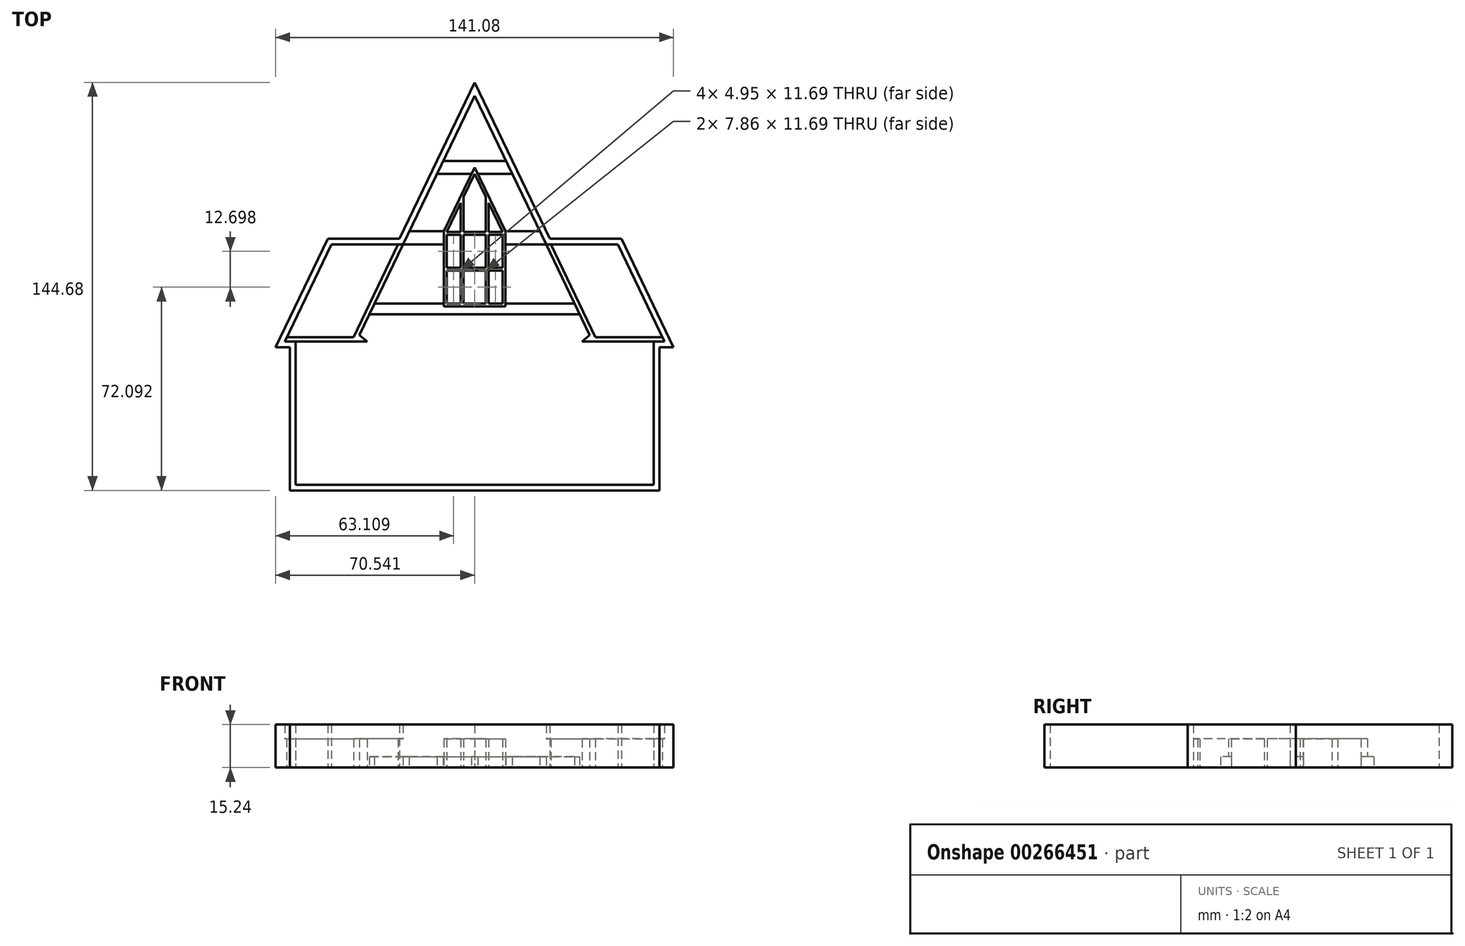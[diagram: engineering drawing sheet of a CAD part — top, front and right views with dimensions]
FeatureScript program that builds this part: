
annotation { "Feature Type Name" : "Feature", "Feature Type Description" : "" }
export const myFeature = defineFeature(function(context is Context, id is Id, definition is map)
    precondition{}
    {
        {
            var Q0;
            Q0=qCreatedBy(makeId("Top.planeOp"),FACE);
            var sketch = newSketch(context, id + "F0", { "sketchPlane" : qUnion([Q0])});
            skLineSegment(sketch, "E0", {"start": v(-58.74, -50.8) * mm, "end": v(68.26, -50.8) * mm});
            skLineSegment(sketch, "E1", {"start": v(-58.74, -50.8) * mm, "end": v(-58.74, 0) * mm});
            skLineSegment(sketch, "E2", {"start": v(68.26, -50.8) * mm, "end": v(68.26, 0) * mm});
            skLineSegment(sketch, "E3", {"start": v(-61.82, 1.52) * mm, "end": v(-46.04, 34.34) * mm});
            skLineSegment(sketch, "E4", {"start": v(-46.04, 34.34) * mm, "end": v(-22.33, 34.34) * mm});
            skLineSegment(sketch, "E5", {"start": v(71.34, 1.52) * mm, "end": v(55.56, 34.34) * mm});
            skLineSegment(sketch, "E6", {"start": v(55.56, 34.34) * mm, "end": v(30.16, 34.34) * mm});
            skLineSegment(sketch, "E7", {"start": v(-20.64, 34.34) * mm, "end": v(-36.05, 2.29) * mm});
            skLineSegment(sketch, "E8", {"start": v(30.16, 34.34) * mm, "end": v(45.57, 2.29) * mm});
            skLineSegment(sketch, "E9", {"start": v(68.26, 0) * mm, "end": v(42.86, 0) * mm});
            skLineSegment(sketch, "E10", {"start": v(42.86, 0) * mm, "end": v(45.57, 2.29) * mm});
            skLineSegment(sketch, "E11", {"start": v(-58.74, 0) * mm, "end": v(-33.34, 0) * mm});
            skLineSegment(sketch, "E12", {"start": v(-33.34, 0) * mm, "end": v(-36.05, 2.29) * mm});
            skLineSegment(sketch, "E13", {"start": v(30.16, 34.34) * mm, "end": v(4.76, 87.16) * mm});
            skLineSegment(sketch, "E14", {"start": v(4.76, 87.16) * mm, "end": v(-20.64, 34.34) * mm});
            skLineSegment(sketch, "E15", {"start": v(4.76, 59.42) * mm, "end": v(0.83, 51.25) * mm});
            skLineSegment(sketch, "E16", {"start": v(4.76, 59.42) * mm, "end": v(8.7, 51.24) * mm});
            skLineSegment(sketch, "E17", {"start": v(14.66, 37.8) * mm, "end": v(14.66, 26.12) * mm});
            skLineSegment(sketch, "E18", {"start": v(-5.15, 37.8) * mm, "end": v(-5.15, 26.12) * mm});
            skLineSegment(sketch, "E19", {"start": v(-5.15, 13.42) * mm, "end": v(-0.2, 13.42) * mm});
            skLineSegment(sketch, "E20", {"start": v(9.71, 13.42) * mm, "end": v(9.71, 25.1) * mm});
            skLineSegment(sketch, "E21", {"start": v(-0.2, 49.12) * mm, "end": v(-0.2, 38.82) * mm});
            skLineSegment(sketch, "E22", {"start": v(14.66, 26.12) * mm, "end": v(9.71, 26.12) * mm});
            skLineSegment(sketch, "E23", {"start": v(14.66, 38.82) * mm, "end": v(9.71, 38.82) * mm});
            skLineSegment(sketch, "E24.0", {"start": v(-58.74, 1.52) * mm, "end": v(-38.11, 1.52) * mm});
            skLineSegment(sketch, "E24.1", {"start": v(-22.33, 34.34) * mm, "end": v(-38.11, 1.52) * mm});
            skLineSegment(sketch, "E25", {"start": v(-58.74, 1.52) * mm, "end": v(-61.82, 1.52) * mm});
            skLineSegment(sketch, "E26.0", {"start": v(68.26, 1.52) * mm, "end": v(47.63, 1.52) * mm});
            skLineSegment(sketch, "E26.1", {"start": v(31.85, 34.34) * mm, "end": v(47.63, 1.52) * mm});
            skLineSegment(sketch, "E27", {"start": v(68.26, 1.52) * mm, "end": v(71.34, 1.52) * mm});
            skLineSegment(sketch, "E28", {"start": v(-22.33, 34.34) * mm, "end": v(-20.64, 34.34) * mm});
            skLineSegment(sketch, "E29", {"start": v(-61.82, 1.52) * mm, "end": v(-62.55, 0) * mm});
            skLineSegment(sketch, "E30", {"start": v(-62.55, 0) * mm, "end": v(-58.74, 0) * mm});
            skLineSegment(sketch, "E31", {"start": v(71.34, 1.52) * mm, "end": v(72.07, 0) * mm});
            skLineSegment(sketch, "E32", {"start": v(68.26, 0) * mm, "end": v(72.07, 0) * mm});
            skLineSegment(sketch, "E33.0", {"start": v(31.44, 36.37) * mm, "end": v(4.76, 91.85) * mm});
            skLineSegment(sketch, "E33.1", {"start": v(56.84, 36.37) * mm, "end": v(31.44, 36.37) * mm});
            skLineSegment(sketch, "E33.2", {"start": v(72.68, 3.42) * mm, "end": v(56.84, 36.37) * mm});
            skLineSegment(sketch, "E33.3", {"start": v(-63.16, 3.42) * mm, "end": v(-65.78, -2.03) * mm});
            skLineSegment(sketch, "E33.4", {"start": v(-63.16, 3.42) * mm, "end": v(-47.32, 36.37) * mm});
            skLineSegment(sketch, "E33.5", {"start": v(-47.32, 36.37) * mm, "end": v(-23.46, 36.37) * mm});
            skLineSegment(sketch, "E33.6", {"start": v(-23.46, 36.37) * mm, "end": v(-21.92, 36.37) * mm});
            skLineSegment(sketch, "E33.7", {"start": v(-65.78, -2.03) * mm, "end": v(-60.77, -2.03) * mm});
            skLineSegment(sketch, "E33.8", {"start": v(-60.77, -52.83) * mm, "end": v(-60.77, -2.03) * mm});
            skLineSegment(sketch, "E33.9", {"start": v(-60.77, -52.83) * mm, "end": v(70.3, -52.83) * mm});
            skLineSegment(sketch, "E33.10", {"start": v(4.76, 91.85) * mm, "end": v(-21.92, 36.37) * mm});
            skLineSegment(sketch, "E33.11", {"start": v(70.3, -52.83) * mm, "end": v(70.3, -2.03) * mm});
            skLineSegment(sketch, "E33.12", {"start": v(70.3, -2.03) * mm, "end": v(75.3, -2.03) * mm});
            skLineSegment(sketch, "E33.13", {"start": v(72.68, 3.42) * mm, "end": v(75.3, -2.03) * mm});
            skLineSegment(sketch, "E34.0", {"start": v(-6.16, 39.05) * mm, "end": v(-6.16, 12.4) * mm});
            skLineSegment(sketch, "E34.1", {"start": v(4.76, 61.76) * mm, "end": v(-6.16, 39.05) * mm});
            skLineSegment(sketch, "E34.2", {"start": v(-6.16, 12.4) * mm, "end": v(15.68, 12.4) * mm});
            skLineSegment(sketch, "E34.3", {"start": v(15.68, 39.05) * mm, "end": v(15.68, 12.4) * mm});
            skLineSegment(sketch, "E34.4", {"start": v(4.76, 61.76) * mm, "end": v(15.68, 39.05) * mm});
            skLineSegment(sketch, "E35", {"start": v(14.66, 37.8) * mm, "end": v(9.71, 37.8) * mm});
            skLineSegment(sketch, "E36", {"start": v(-5.15, 25.1) * mm, "end": v(-0.2, 25.1) * mm});
            skLineSegment(sketch, "E37", {"start": v(0.83, 13.42) * mm, "end": v(0.83, 25.1) * mm});
            skLineSegment(sketch, "E38", {"start": v(9.71, 13.42) * mm, "end": v(8.7, 13.42) * mm});
            skLineSegment(sketch, "E39", {"start": v(8.7, 13.42) * mm, "end": v(8.7, 25.1) * mm});
            skLineSegment(sketch, "E40.trimOffspring", {"start": v(-0.2, 49.12) * mm, "end": v(-5.15, 38.82) * mm});
            skLineSegment(sketch, "E41.trimOffspring", {"start": v(9.71, 49.12) * mm, "end": v(14.66, 38.82) * mm});
            skLineSegment(sketch, "E42.trimOffspring", {"start": v(-0.2, 37.8) * mm, "end": v(-0.2, 26.12) * mm});
            skLineSegment(sketch, "E43.trimOffspring", {"start": v(-0.2, 38.82) * mm, "end": v(-5.15, 38.82) * mm});
            skLineSegment(sketch, "E44.trimOffspring", {"start": v(0.83, 38.82) * mm, "end": v(0.83, 51.25) * mm});
            skLineSegment(sketch, "E45.trimOffspring", {"start": v(-0.2, 37.8) * mm, "end": v(-5.15, 37.8) * mm});
            skLineSegment(sketch, "E46.trimOffspring", {"start": v(8.7, 38.82) * mm, "end": v(8.7, 51.24) * mm});
            skLineSegment(sketch, "E47.trimOffspring", {"start": v(8.7, 38.82) * mm, "end": v(0.83, 38.82) * mm});
            skLineSegment(sketch, "E48.trimOffspring", {"start": v(9.71, 38.82) * mm, "end": v(9.71, 49.12) * mm});
            skLineSegment(sketch, "E49.trimOffspring", {"start": v(8.7, 37.8) * mm, "end": v(0.83, 37.8) * mm});
            skLineSegment(sketch, "E50.trimOffspring", {"start": v(14.66, 25.1) * mm, "end": v(14.66, 13.42) * mm});
            skLineSegment(sketch, "E51.trimOffspring", {"start": v(9.71, 26.12) * mm, "end": v(9.71, 37.8) * mm});
            skLineSegment(sketch, "E52.trimOffspring", {"start": v(8.7, 26.12) * mm, "end": v(8.7, 37.8) * mm});
            skLineSegment(sketch, "E53.trimOffspring", {"start": v(0.83, 26.12) * mm, "end": v(0.83, 37.8) * mm});
            skLineSegment(sketch, "E54.trimOffspring", {"start": v(-0.2, 25.1) * mm, "end": v(-0.2, 13.42) * mm});
            skLineSegment(sketch, "E55.trimOffspring", {"start": v(-5.15, 25.1) * mm, "end": v(-5.15, 13.42) * mm});
            skLineSegment(sketch, "E56.trimOffspring", {"start": v(-0.2, 26.12) * mm, "end": v(-5.15, 26.12) * mm});
            skLineSegment(sketch, "E57.trimOffspring", {"start": v(0.83, 25.1) * mm, "end": v(8.7, 25.1) * mm});
            skLineSegment(sketch, "E58.trimOffspring", {"start": v(8.7, 26.12) * mm, "end": v(0.83, 26.12) * mm});
            skLineSegment(sketch, "E59.trimOffspring", {"start": v(9.71, 25.1) * mm, "end": v(14.66, 25.1) * mm});
            skLineSegment(sketch, "E60.trimOffspring", {"start": v(9.71, 13.42) * mm, "end": v(14.66, 13.42) * mm});
            skLineSegment(sketch, "E61.trimOffspring", {"start": v(0.83, 13.42) * mm, "end": v(8.7, 13.42) * mm});
            skLineSegment(sketch, "E62", {"start": v(-8.58, 59.42) * mm, "end": v(18.1, 59.42) * mm});
            skLineSegment(sketch, "E63", {"start": v(-18.38, 39.05) * mm, "end": v(-6.16, 39.05) * mm});
            skLineSegment(sketch, "E64", {"start": v(-20.64, 34.34) * mm, "end": v(-6.16, 34.34) * mm});
            skLineSegment(sketch, "E65", {"start": v(15.68, 39.05) * mm, "end": v(27.9, 39.05) * mm});
            skLineSegment(sketch, "E66", {"start": v(30.16, 34.34) * mm, "end": v(15.68, 34.34) * mm});
            skLineSegment(sketch, "E67", {"start": v(40.22, 13.42) * mm, "end": v(-30.7, 13.42) * mm});
            skLineSegment(sketch, "E68", {"start": v(-32.53, 9.6) * mm, "end": v(42.05, 9.6) * mm});
            skLineSegment(sketch, "E69", {"start": v(-6.4, 63.98) * mm, "end": v(15.9, 63.98) * mm});
            skSolve(sketch);
        }
        {
            var Q0;
            Q0=makeQuery(id+"F0.imprint","IMPRINT",FACE,{"disambiguationData":[TD([[makeQuery(id+"F0.imprint","IMPRINT",EDGE,{"derivedFrom":sQuery(id+"F0.wireOp",EDGE,"E0")}),-1.0]])]});
            extrude(context, id + "F1", {"entities" : qUnion([Q0]), "depth" : 15.24 * mm});
        }
        {
            var Q0;
            Q0=makeQuery(id+"F0.imprint","IMPRINT",FACE,{"disambiguationData":[TD([[makeQuery(id+"F0.imprint","IMPRINT",EDGE,{"derivedFrom":sQuery(id+"F0.wireOp",EDGE,"E7")}),-1.0]])]});
            var Q1;
            {var subQ1=sQuery(id+"F0.wireOp",EDGE,"E8");Q1=makeQuery(id+"F0.imprint","IMPRINT",FACE,{"disambiguationData":[TD([[makeQuery(id+"F0.imprint","IMPRINT",EDGE,{"derivedFrom":subQ1}),1.0]])]});}
            extrude(context, id + "F2", {"entities" : qUnion([Q0, Q1]), "operationType" : NewBodyOperationType.ADD, "depth" : 10.16 * mm});
        }
        {
            var Q0;
            Q0=makeQuery(id+"F0.imprint","IMPRINT",FACE,{"disambiguationData":[TD([[makeQuery(id+"F0.imprint","IMPRINT",EDGE,{"derivedFrom":sQuery(id+"F0.wireOp",EDGE,"E15")}),-1.0]])]});
            var Q1;
            {var subQ0=sQuery(id+"F0.wireOp",EDGE,"E34.4");var subQ1=sQuery(id+"F0.wireOp",EDGE,"E34.1");var subQ2=makeQuery(id+"F0.imprint","INTERSECT",VERTEX,{"derivedFrom":[subQ1,subQ0]});Q1=makeQuery(id+"F0.imprint","IMPRINT",FACE,{"disambiguationData":[TD([[makeQuery(id+"F0.imprint","IMPRINT",EDGE,{"disambiguationData":[TD([[subQ2,-1.0]])],"derivedFrom":subQ1}),1.0]])]});}
            var Q2;
            {var subQ1=sQuery(id+"F0.wireOp",EDGE,"E34.2");Q2=makeQuery(id+"F0.imprint","IMPRINT",FACE,{"disambiguationData":[TD([[makeQuery(id+"F0.imprint","IMPRINT",EDGE,{"derivedFrom":subQ1}),1.0]])]});}
            extrude(context, id + "F3", {"entities" : qUnion([Q0, Q1, Q2]), "depth" : 10.16 * mm});
        }
        {
            var Q0;
            {var subQ0=sQuery(id+"F0.wireOp",EDGE,"E34.2");Q0=makeQuery(id+"F0.imprint","IMPRINT",FACE,{"disambiguationData":[TD([[makeQuery(id+"F0.imprint","IMPRINT",EDGE,{"derivedFrom":subQ0}),-1.0]])]});}
            var Q1;
            {var subQ2=sQuery(id+"F0.wireOp",EDGE,"E63");Q1=makeQuery(id+"F0.imprint","IMPRINT",FACE,{"disambiguationData":[TD([[makeQuery(id+"F0.imprint","IMPRINT",EDGE,{"derivedFrom":subQ2}),-1.0]])]});}
            var Q2;
            {var subQ2=sQuery(id+"F0.wireOp",EDGE,"E65");Q2=makeQuery(id+"F0.imprint","IMPRINT",FACE,{"disambiguationData":[TD([[makeQuery(id+"F0.imprint","IMPRINT",EDGE,{"derivedFrom":subQ2}),-1.0]])]});}
            var Q3;
            {var subQ8=sQuery(id+"F0.wireOp",EDGE,"S1RluHXZ-Pm47-1miD-Gq6c-9LfcvvD9yspV");Q3=makeQuery(id+"F0.imprint","IMPRINT",FACE,{"disambiguationData":[TD([[makeQuery(id+"F0.imprint","IMPRINT",EDGE,{"derivedFrom":subQ8}),-1.0]])]});}
            var Q4;
            {var subQ6=sQuery(id+"F0.wireOp",EDGE,"E69");Q4=makeQuery(id+"F0.imprint","IMPRINT",FACE,{"disambiguationData":[TD([[makeQuery(id+"F0.imprint","IMPRINT",EDGE,{"derivedFrom":subQ6}),-1.0]])]});}
            extrude(context, id + "F4", {"entities" : qUnion([Q0, Q1, Q2, Q3, Q4]), "operationType" : NewBodyOperationType.ADD, "depth" : 3.8 * mm});
        }
    });
